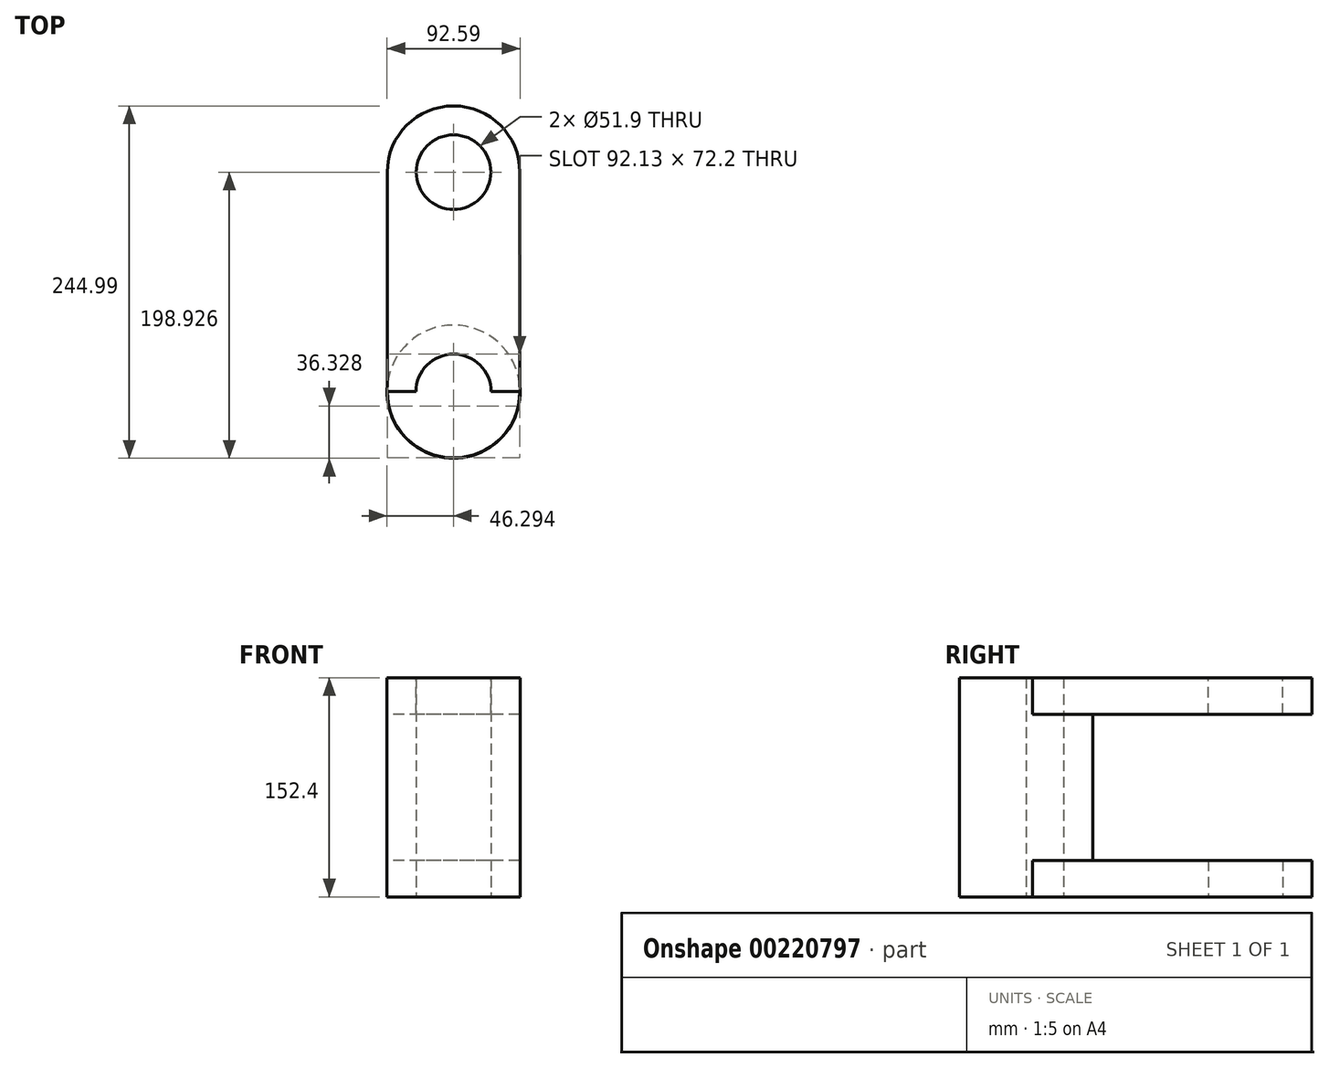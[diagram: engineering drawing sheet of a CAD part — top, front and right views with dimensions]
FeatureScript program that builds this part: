
annotation { "Feature Type Name" : "Feature", "Feature Type Description" : "" }
export const myFeature = defineFeature(function(context is Context, id is Id, definition is map)
    precondition{}
    {
        {
            var Q0;
            Q0=qCreatedBy(makeId("Top.planeOp"),FACE);
            var sketch = newSketch(context, id + "F0", { "sketchPlane" : qUnion([Q0])});
            skLineSegment(sketch, "E0.bottom", {"start": v(-43.64, 76.55) * mm, "end": v(48.5, 76.55) * mm});
            skLineSegment(sketch, "E0.top", {"start": v(-43.64, -76.08) * mm, "end": v(48.5, -76.08) * mm});
            skLineSegment(sketch, "E0.left", {"start": v(-43.64, 76.55) * mm, "end": v(-43.64, -76.08) * mm});
            skLineSegment(sketch, "E0.right", {"start": v(48.5, 76.55) * mm, "end": v(48.5, -76.08) * mm});
            skArc(sketch, "E1", {"start": v(48.5, 76.55) * mm, "mid": v(2.42, 122.61) * mm, "end": v(-43.64, 76.55) * mm});
            skArc(sketch, "E2", {"start": v(48.5, -76.08) * mm, "mid": v(2.42, -122.15) * mm, "end": v(-43.64, -76.08) * mm});
            skCircle(sketch, "E3", {"center": v(2.42, 76.55) * mm, "radius": 25.95 * mm});
            skCircle(sketch, "E4", {"center": v(2.42, -76.08) * mm, "radius": 26.13 * mm});
            skCircle(sketch, "E5", {"center": v(2.42, -76.08) * mm, "radius": 46.3 * mm});
            skSolve(sketch);
        }
        {
            var Q0;
            {var subQ2=sQuery(id+"F0.wireOp",EDGE,"E0.top");var subQ9=sQuery(id+"F0.wireOp",EDGE,"E4");var subQ10=makeQuery(id+"F0.imprint","INTERSECT",VERTEX,{"disambiguationData":[OD(0.0)],"derivedFrom":[subQ2,subQ9]});Q0=makeQuery(id+"F0.imprint","IMPRINT",FACE,{"disambiguationData":[TD([[makeQuery(id+"F0.imprint","IMPRINT",EDGE,{"disambiguationData":[TD([[subQ10,1.0]])],"derivedFrom":subQ9}),-1.0]])]});}
            var Q1;
            {var subQ0=sQuery(id+"F0.wireOp",EDGE,"E2");Q1=makeQuery(id+"F0.imprint","IMPRINT",FACE,{"disambiguationData":[TD([[makeQuery(id+"F0.imprint","IMPRINT",EDGE,{"derivedFrom":subQ0}),-1.0]])]});}
            extrude(context, id + "F1", {"entities" : qUnion([Q0, Q1]), "depth" : 76.2 * mm});
        }
        {
            var Q0;
            Q0 = qSketchRegion(id + "F0", true);
            extrude(context, id + "F2", {"entities" : qUnion([Q0]), "operationType" : NewBodyOperationType.ADD, "depth" : 25.4 * mm});
        }
        {
            var Q0;
            Q0=makeQuery(id+"F1.opExtrude","SWEPT_BODY",BODY,{"disambiguationData":[OSD([sQuery(id+"F0.wireOp",EDGE,"E0.left"),sQuery(id+"F0.wireOp",EDGE,"E0.right"),sQuery(id+"F0.wireOp",EDGE,"E2"),sQuery(id+"F0.wireOp",EDGE,"E4"),sQuery(id+"F0.wireOp",EDGE,"E5")])]});
            var Q1;
            Q1=makeQuery(id+"F1.opExtrude","CAP_FACE",FACE,{"disambiguationData":[OSD([sQuery(id+"F0.wireOp",EDGE,"E0.left"),sQuery(id+"F0.wireOp",EDGE,"E0.right"),sQuery(id+"F0.wireOp",EDGE,"E2"),sQuery(id+"F0.wireOp",EDGE,"E4"),sQuery(id+"F0.wireOp",EDGE,"E5")])],"isStart":false});
            mirror(context, id + "F3", {"operationType" : NewBodyOperationType.ADD, "entities" : qUnion([Q0]), "mirrorPlane" : qUnion([Q1])});
        }
    });
